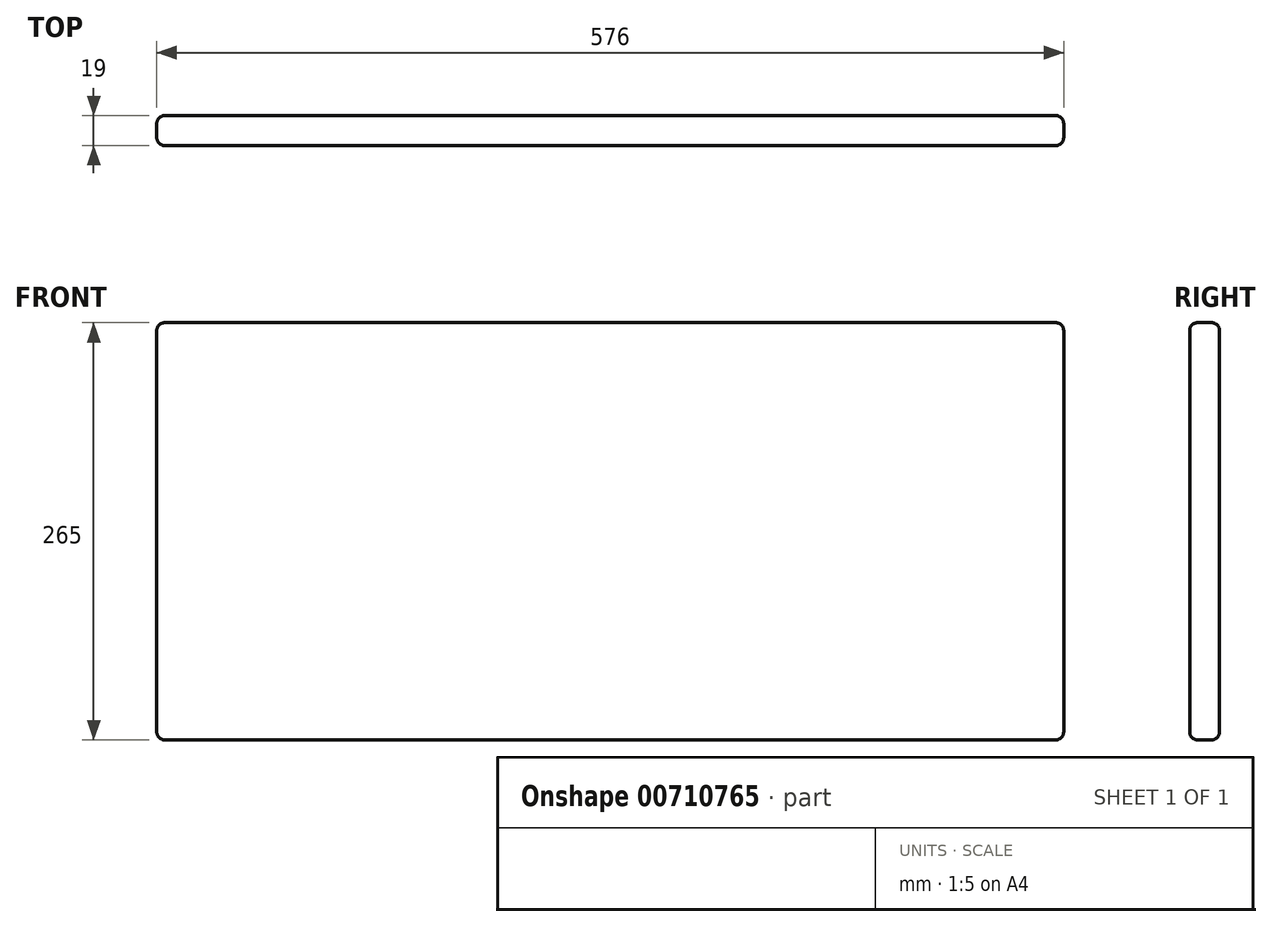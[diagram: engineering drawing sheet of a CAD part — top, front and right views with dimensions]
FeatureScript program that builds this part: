
annotation { "Feature Type Name" : "Feature", "Feature Type Description" : "" }
export const myFeature = defineFeature(function(context is Context, id is Id, definition is map)
    precondition{}
    {
        {
            var Q0;
            Q0=qCreatedBy(makeId("Front.planeOp"),FACE);
            var sketch = newSketch(context, id + "F0", { "sketchPlane" : qUnion([Q0])});
            skLineSegment(sketch, "E0.bottom", {"start": v(-295.59, 116.15) * mm, "end": v(280.41, 116.15) * mm});
            skLineSegment(sketch, "E0.top", {"start": v(-295.59, -148.85) * mm, "end": v(280.41, -148.85) * mm});
            skLineSegment(sketch, "E0.left", {"start": v(-295.59, 116.15) * mm, "end": v(-295.59, -148.85) * mm});
            skLineSegment(sketch, "E0.right", {"start": v(280.41, 116.15) * mm, "end": v(280.41, -148.85) * mm});
            skSolve(sketch);
        }
        {
            var Q0;
            Q0=makeQuery(id+"F0.imprint","IMPRINT",FACE,{"disambiguationData":[TD([[makeQuery(id+"F0.imprint","IMPRINT",EDGE,{"derivedFrom":sQuery(id+"F0.wireOp",EDGE,"E0.bottom")}),-1.0]])]});
            extrude(context, id + "F1", {"entities" : qUnion([Q0]), "depth" : 19 * mm, "offsetDistance" : 25 * mm});
        }
        {
            var Q0;
            Q0=makeQuery(id+"F1.opExtrude","SWEPT_EDGE",EDGE,{"disambiguationData":[OSD([sQuery(id+"F0.wireOp",EDGE,"E0.bottom"),sQuery(id+"F0.wireOp",EDGE,"E0.left")])]});
            var Q1;
            Q1=makeQuery(id+"F1.opExtrude","SWEPT_EDGE",EDGE,{"disambiguationData":[OSD([sQuery(id+"F0.wireOp",EDGE,"E0.bottom"),sQuery(id+"F0.wireOp",EDGE,"E0.right")])]});
            var Q2;
            Q2=makeQuery(id+"F1.opExtrude","SWEPT_EDGE",EDGE,{"disambiguationData":[OSD([sQuery(id+"F0.wireOp",EDGE,"E0.top"),sQuery(id+"F0.wireOp",EDGE,"E0.right")])]});
            var Q3;
            Q3=makeQuery(id+"F1.opExtrude","CAP_EDGE",EDGE,{"disambiguationData":[OSD([sQuery(id+"F0.wireOp",EDGE,"E0.bottom")])],"isStart":true});
            var Q4;
            Q4=makeQuery(id+"F1.opExtrude","CAP_EDGE",EDGE,{"disambiguationData":[OSD([sQuery(id+"F0.wireOp",EDGE,"E0.bottom")])],"isStart":false});
            var Q5;
            Q5=makeQuery(id+"F1.opExtrude","CAP_EDGE",EDGE,{"disambiguationData":[OSD([sQuery(id+"F0.wireOp",EDGE,"E0.top")])],"isStart":false});
            var Q6;
            Q6=makeQuery(id+"F1.opExtrude","SWEPT_EDGE",EDGE,{"disambiguationData":[OSD([sQuery(id+"F0.wireOp",EDGE,"E0.top"),sQuery(id+"F0.wireOp",EDGE,"E0.left")])]});
            var Q7;
            Q7=makeQuery(id+"F1.opExtrude","CAP_EDGE",EDGE,{"disambiguationData":[OSD([sQuery(id+"F0.wireOp",EDGE,"E0.top")])],"isStart":true});
            var Q8;
            Q8=makeQuery(id+"F1.opExtrude","CAP_EDGE",EDGE,{"disambiguationData":[OSD([sQuery(id+"F0.wireOp",EDGE,"E0.right")])],"isStart":false});
            var Q9;
            Q9=makeQuery(id+"F1.opExtrude","CAP_EDGE",EDGE,{"disambiguationData":[OSD([sQuery(id+"F0.wireOp",EDGE,"E0.left")])],"isStart":false});
            var Q10;
            Q10=makeQuery(id+"F1.opExtrude","CAP_EDGE",EDGE,{"disambiguationData":[OSD([sQuery(id+"F0.wireOp",EDGE,"E0.right")])],"isStart":true});
            var Q11;
            Q11=makeQuery(id+"F1.opExtrude","CAP_EDGE",EDGE,{"disambiguationData":[OSD([sQuery(id+"F0.wireOp",EDGE,"E0.left")])],"isStart":true});
            fillet(context, id + "F2", {"entities" : qUnion([Q0, Q1, Q2, Q3, Q4, Q5, Q6, Q7, Q8, Q9, Q10, Q11]), "radius" : 5 * mm, "tangentPropagation" : true, "allowEdgeOverflow" : false});
        }
    });
